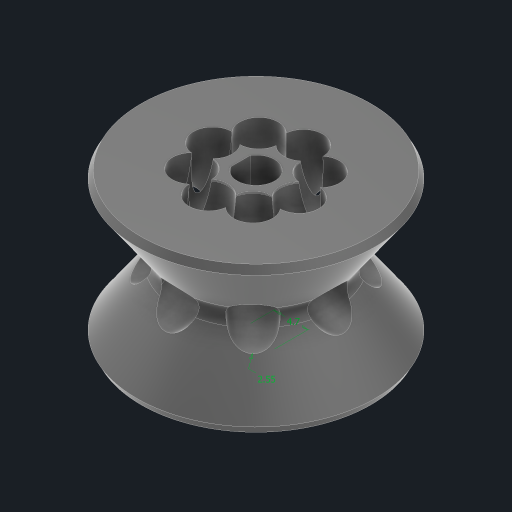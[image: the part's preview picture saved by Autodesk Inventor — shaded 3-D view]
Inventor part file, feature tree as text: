
AUTODESK INVENTOR PART (.ipt)
format: ipt  version: 2023 (Build 270158000, 158)  size: 726,528 bytes
history: native  units: mm
features: sketch x3, chamfer x3, plane x2, revolve x1, extrude x1, sweep x1, fillet x1, hole x1, pattern_circular x1
ambient origin geometry x8: Origin, YZ Plane, XZ Plane, XY Plane, X Axis, Y Axis, Z Axis, Center Point
bodies: Solid1 (feature_tree)
feature tree (14):
  sketch  "Sketch1"  dims[d1=4.7mm d4=20.0mm]
  revolve  "Revolution1"  [1 undecoded]
  extrude  "Extrusion1"  Depth=14.0mm
  chamfer  "Chamfer1"  [1 undecoded]
  plane  "Work Plane3"
  sweep  "Sweep1"
  plane  "Work Plane4"
  fillet  "Fillet1"  Radius=3.490659mm
  chamfer  "Chamfer2"  [1 undecoded]
  hole  "Hole4"  [1 undecoded]
  chamfer  "Chamfer3"  [1 undecoded]
  pattern_circular  "Circular Pattern1"  [2 undecoded]
  sketch  "Sketch8"  dims[d5=14.0mm d6=14.0mm]
  sketch  "Sketch9"  dims[d7=90.0deg d8=0.0mm d9=0.0mm d10=1.2mm d11=2.0mm d12=45.0deg d15=30.0deg d20=3.490659mm d71=-12.0mm d72=5.3mm d73=0.0mm d74=0.0mm d92=2.55mm d93=10.0mm d95=2.0mm d98=1.0mm d99=2.0mm d100=45.0deg d102=9.599311mm d103=10.0mm d105=6.5mm d106=6.0mm d107=6.0mm d108=2.0mm d109=90.0deg d110=5.3mm d111=0.0mm d112=0.2mm d113=2.0mm d114=45.0deg d117=80.0mm d118=360.0deg]
note: 7 required parameter values undecoded (feature->parameter linkage not recoverable at this tier; creation-order binding heuristic only, values carry confidence <= 0.55)